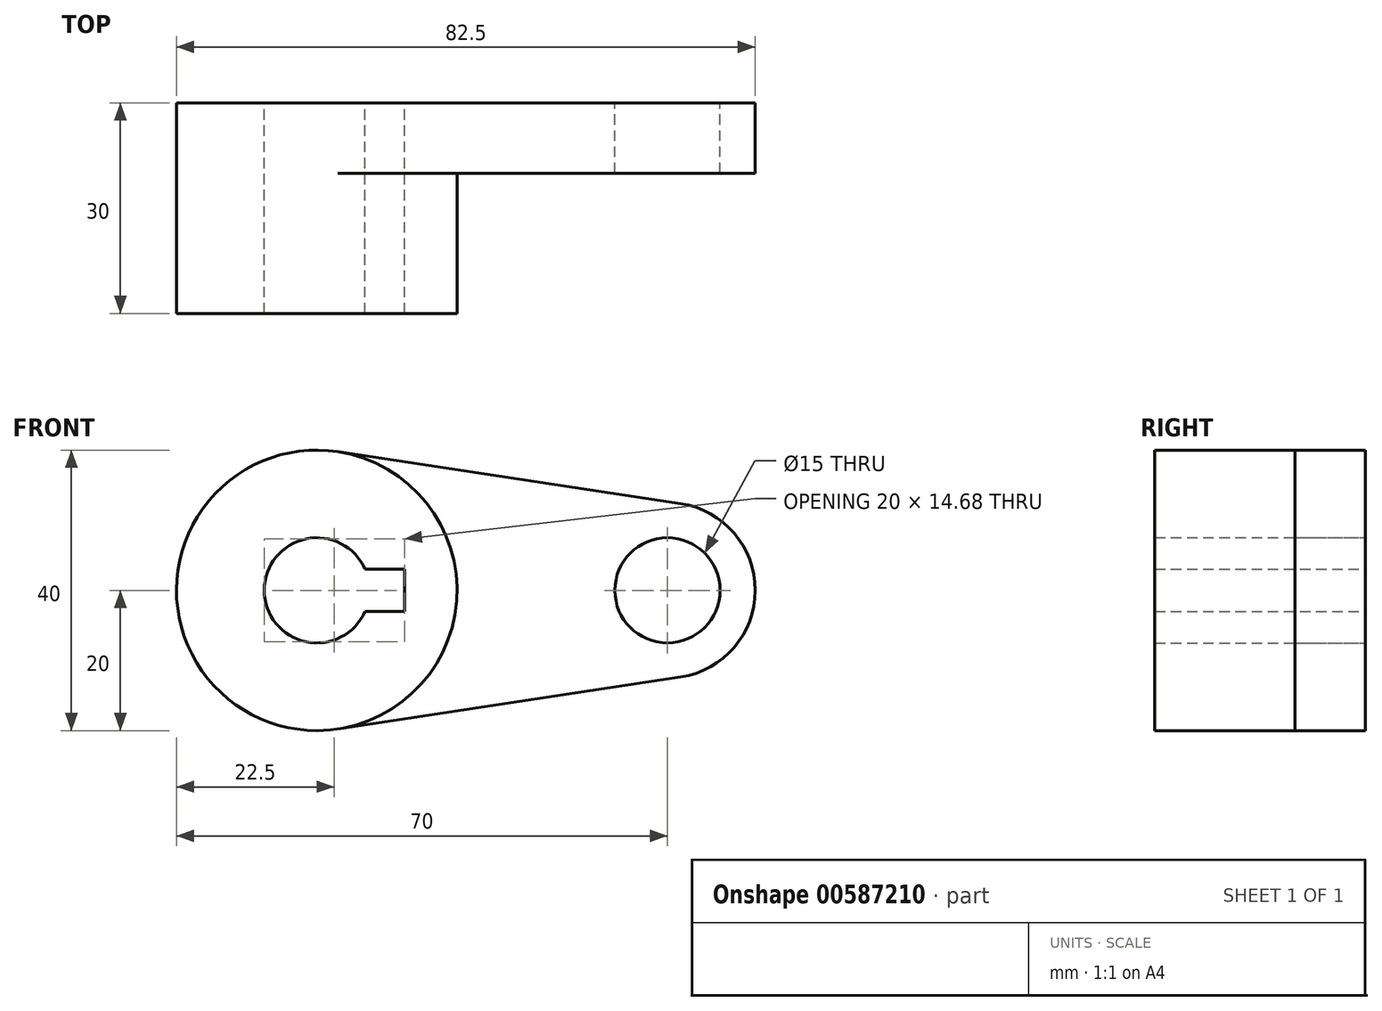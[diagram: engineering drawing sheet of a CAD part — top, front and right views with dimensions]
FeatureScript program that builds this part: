
annotation { "Feature Type Name" : "Feature", "Feature Type Description" : "" }
export const myFeature = defineFeature(function(context is Context, id is Id, definition is map)
    precondition{}
    {
        {
            var Q0;
            Q0=qCreatedBy(makeId("Front.planeOp"),FACE);
            var sketch = newSketch(context, id + "F0", { "sketchPlane" : qUnion([Q0])});
            skCircle(sketch, "E0", {"center": v(0, 0) * mm, "radius": 20 * mm});
            skCircle(sketch, "E1", {"center": v(50, 0) * mm, "radius": 12.5 * mm});
            skLineSegment(sketch, "E2", {"start": v(3, 19.77) * mm, "end": v(51.88, 12.36) * mm});
            skLineSegment(sketch, "E3", {"start": v(3, -19.77) * mm, "end": v(51.88, -12.36) * mm});
            skLineSegment(sketch, "E4.bottom", {"start": v(12.5, -3) * mm, "end": v(-12.5, -3) * mm});
            skLineSegment(sketch, "E4.top", {"start": v(12.5, 3) * mm, "end": v(-12.5, 3) * mm});
            skLineSegment(sketch, "E4.left", {"start": v(12.5, -3) * mm, "end": v(12.5, 3) * mm});
            skLineSegment(sketch, "E4.right", {"start": v(-12.5, -3) * mm, "end": v(-12.5, 3) * mm});
            skCircle(sketch, "E5", {"center": v(0, 0) * mm, "radius": 7.5 * mm});
            skCircle(sketch, "E6", {"center": v(50, 0) * mm, "radius": 7.5 * mm});
            skSolve(sketch);
        }
        {
            var Q0;
            {var subQ4=sQuery(id+"F0.wireOp",EDGE,"E4.left");Q0=makeQuery(id+"F0.imprint","IMPRINT",FACE,{"disambiguationData":[TD([[makeQuery(id+"F0.imprint","IMPRINT",EDGE,{"derivedFrom":subQ4}),-1.0]])]});}
            var Q1;
            {var subQ0=sQuery(id+"F0.wireOp",EDGE,"E2");Q1=makeQuery(id+"F0.imprint","IMPRINT",FACE,{"disambiguationData":[TD([[makeQuery(id+"F0.imprint","IMPRINT",EDGE,{"derivedFrom":subQ0}),-1.0]])]});}
            var Q2;
            Q2=makeQuery(id+"F0.imprint","IMPRINT",FACE,{"disambiguationData":[TD([[makeQuery(id+"F0.imprint","IMPRINT",EDGE,{"derivedFrom":sQuery(id+"F0.wireOp",EDGE,"E6")}),-1.0]])]});
            var Q3;
            {var subQ0=sQuery(id+"F0.wireOp",EDGE,"E4.right");Q3=makeQuery(id+"F0.imprint","IMPRINT",FACE,{"disambiguationData":[TD([[makeQuery(id+"F0.imprint","IMPRINT",EDGE,{"derivedFrom":subQ0}),-1.0]])]});}
            extrude(context, id + "F1", {"entities" : qUnion([Q0, Q1, Q2, Q3]), "depth" : 10 * mm, "offsetDistance" : 25 * mm});
        }
        {
            var Q0;
            {var subQ4=sQuery(id+"F0.wireOp",EDGE,"E4.left");Q0=makeQuery(id+"F0.imprint","IMPRINT",FACE,{"disambiguationData":[TD([[makeQuery(id+"F0.imprint","IMPRINT",EDGE,{"derivedFrom":subQ4}),-1.0]])]});}
            var Q1;
            {var subQ0=sQuery(id+"F0.wireOp",EDGE,"E4.right");Q1=makeQuery(id+"F0.imprint","IMPRINT",FACE,{"disambiguationData":[TD([[makeQuery(id+"F0.imprint","IMPRINT",EDGE,{"derivedFrom":subQ0}),-1.0]])]});}
            extrude(context, id + "F2", {"entities" : qUnion([Q0, Q1]), "operationType" : NewBodyOperationType.ADD, "depth" : 30 * mm, "offsetDistance" : 25 * mm});
        }
    });
